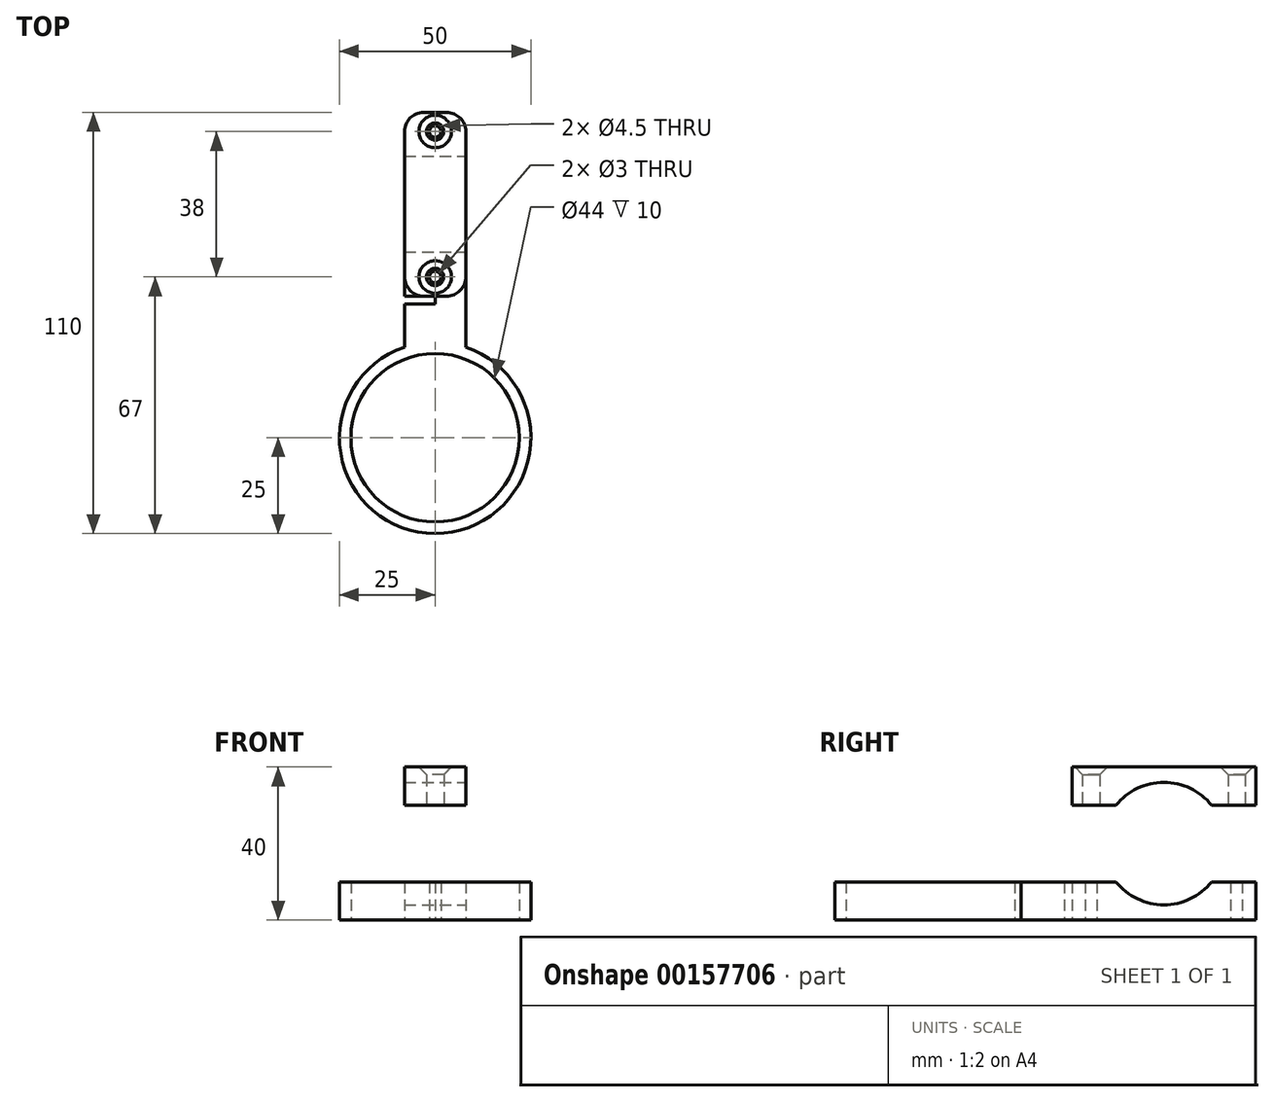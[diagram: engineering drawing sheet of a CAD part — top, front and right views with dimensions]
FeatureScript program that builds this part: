
annotation { "Feature Type Name" : "Feature", "Feature Type Description" : "" }
export const myFeature = defineFeature(function(context is Context, id is Id, definition is map)
    precondition{}
    {
        {
            var Q0;
            Q0=qCreatedBy(makeId("Top.planeOp"),FACE);
            var sketch = newSketch(context, id + "F0", { "sketchPlane" : qUnion([Q0])});
            skCircle(sketch, "E0", {"center": v(0, -25) * mm, "radius": 25 * mm});
            skLineSegment(sketch, "E1", {"start": v(0, 0) * mm, "end": v(0, 10) * mm});
            skLineSegment(sketch, "E2", {"start": v(0, 10) * mm, "end": v(-8, 10) * mm});
            skLineSegment(sketch, "E3", {"start": v(-8, 10) * mm, "end": v(-8, -1.31) * mm});
            skLineSegment(sketch, "E4.MirrorCS", {"start": v(4, 10) * mm, "end": v(8, 10) * mm});
            skLineSegment(sketch, "E5.MirrorCS", {"start": v(8, 10) * mm, "end": v(8, -1.31) * mm});
            skCircle(sketch, "E6", {"center": v(0, -25) * mm, "radius": 22 * mm});
            skLineSegment(sketch, "E7", {"start": v(4, 10) * mm, "end": v(4, -3.37) * mm});
            skLineSegment(sketch, "E8", {"start": v(0, -3) * mm, "end": v(0, 0) * mm});
            skPoint(sketch, "E9", {"position": v(4, 10) * mm});
            skPoint(sketch, "E10.orphan", {"position": v(0, 10) * mm});
            skLineSegment(sketch, "E11.bottom", {"start": v(-8, 10) * mm, "end": v(0, 10) * mm});
            skLineSegment(sketch, "E11.top", {"start": v(-8, 12) * mm, "end": v(0, 12) * mm});
            skLineSegment(sketch, "E11.left", {"start": v(-8, 10) * mm, "end": v(-8, 12) * mm});
            skLineSegment(sketch, "E11.right", {"start": v(0, 10) * mm, "end": v(0, 12) * mm});
            skLineSegment(sketch, "E12.bottom", {"start": v(-8, 12) * mm, "end": v(8, 12) * mm});
            skLineSegment(sketch, "E12.top", {"start": v(-8, 60) * mm, "end": v(8, 60) * mm});
            skLineSegment(sketch, "E12.left", {"start": v(-8, 12) * mm, "end": v(-8, 60) * mm});
            skLineSegment(sketch, "E12.right", {"start": v(8, 12) * mm, "end": v(8, 60) * mm});
            skLineSegment(sketch, "E13", {"start": v(-8, 17) * mm, "end": v(8, 17) * mm});
            skLineSegment(sketch, "E14", {"start": v(-8, 36) * mm, "end": v(8, 36) * mm, "construction": true});
            skLineSegment(sketch, "E15.MirrorCS", {"start": v(-8, 55) * mm, "end": v(8, 55) * mm});
            skCircle(sketch, "E16", {"center": v(0, 55) * mm, "radius": 1.5 * mm});
            skCircle(sketch, "E17.MirrorC", {"center": v(0, 17) * mm, "radius": 1.5 * mm});
            skCircle(sketch, "E18", {"center": v(0, 55) * mm, "radius": 2.25 * mm});
            skCircle(sketch, "E19.MirrorC", {"center": v(0, 17) * mm, "radius": 2.25 * mm});
            skLineSegment(sketch, "E20", {"start": v(8, 10) * mm, "end": v(8, 12) * mm});
            skSolve(sketch);
        }
        {
            var Q0;
            {var subQ0=sQuery(id+"F0.wireOp",EDGE,"E1");Q0=makeQuery(id+"F0.imprint","IMPRINT",FACE,{"disambiguationData":[TD([[makeQuery(id+"F0.imprint","IMPRINT",EDGE,{"derivedFrom":subQ0}),1.0]])]});}
            var Q1;
            {var subQ4=sQuery(id+"F0.wireOp",EDGE,"E4.MirrorCS");Q1=makeQuery(id+"F0.imprint","IMPRINT",FACE,{"disambiguationData":[TD([[makeQuery(id+"F0.imprint","IMPRINT",EDGE,{"derivedFrom":subQ4}),-1.0]])]});}
            var Q2;
            {var subQ3=sQuery(id+"F0.wireOp",EDGE,"E8");Q2=makeQuery(id+"F0.imprint","IMPRINT",FACE,{"disambiguationData":[TD([[makeQuery(id+"F0.imprint","IMPRINT",EDGE,{"derivedFrom":subQ3}),1.0]])]});}
            var Q3;
            {var subQ5=sQuery(id+"F0.wireOp",EDGE,"E1");Q3=makeQuery(id+"F0.imprint","IMPRINT",FACE,{"disambiguationData":[TD([[makeQuery(id+"F0.imprint","IMPRINT",EDGE,{"derivedFrom":subQ5}),-1.0]])]});}
            var Q4;
            {var subQ0=sQuery(id+"F0.wireOp",EDGE,"E8");Q4=makeQuery(id+"F0.imprint","IMPRINT",FACE,{"disambiguationData":[TD([[makeQuery(id+"F0.imprint","IMPRINT",EDGE,{"derivedFrom":subQ0}),-1.0]])]});}
            extrude(context, id + "F1", {"entities" : qUnion([Q0, Q1, Q2, Q3, Q4]), "depth" : 10 * mm, "offsetDistance" : 25 * mm});
        }
        {
            var Q0;
            {var subQ0=sQuery(id+"F0.wireOp",EDGE,"E12.top");Q0=makeQuery(id+"F0.imprint","IMPRINT",FACE,{"disambiguationData":[TD([[makeQuery(id+"F0.imprint","IMPRINT",EDGE,{"derivedFrom":subQ0}),-1.0]])]});}
            var Q1;
            {var subQ0=sQuery(id+"F0.wireOp",EDGE,"E13");Q1=makeQuery(id+"F0.imprint","IMPRINT",FACE,{"disambiguationData":[TD([[makeQuery(id+"F0.imprint","IMPRINT",EDGE,{"derivedFrom":subQ0}),1.0]])]});}
            var Q2;
            {var subQ3=sQuery(id+"F0.wireOp",EDGE,"E13");Q2=makeQuery(id+"F0.imprint","IMPRINT",FACE,{"disambiguationData":[TD([[makeQuery(id+"F0.imprint","IMPRINT",EDGE,{"derivedFrom":subQ3}),-1.0]])]});}
            var Q3;
            Q3=makeQuery(id+"F0.imprint","IMPRINT",FACE,{"disambiguationData":[TD([[makeQuery(id+"F0.imprint","IMPRINT",EDGE,{"derivedFrom":sQuery(id+"F0.wireOp",EDGE,"E11.bottom")}),1.0]])]});
            var Q4;
            {var subQ0=sQuery(id+"F0.wireOp",EDGE,"E18");var subQ1=sQuery(id+"F0.wireOp",EDGE,"E15.MirrorCS");var subQ2=makeQuery(id+"F0.imprint","INTERSECT",VERTEX,{"disambiguationData":[OD(0.0)],"derivedFrom":[subQ1,subQ0]});Q4=makeQuery(id+"F0.imprint","IMPRINT",FACE,{"disambiguationData":[TD([[makeQuery(id+"F0.imprint","IMPRINT",EDGE,{"disambiguationData":[TD([[subQ2,-1.0]])],"derivedFrom":subQ1}),-1.0]])]});}
            var Q5;
            {var subQ0=sQuery(id+"F0.wireOp",EDGE,"E18");var subQ1=sQuery(id+"F0.wireOp",EDGE,"E15.MirrorCS");var subQ2=makeQuery(id+"F0.imprint","INTERSECT",VERTEX,{"disambiguationData":[OD(0.0)],"derivedFrom":[subQ1,subQ0]});Q5=makeQuery(id+"F0.imprint","IMPRINT",FACE,{"disambiguationData":[TD([[makeQuery(id+"F0.imprint","IMPRINT",EDGE,{"disambiguationData":[TD([[subQ2,-1.0]])],"derivedFrom":subQ1}),1.0]])]});}
            var Q6;
            {var subQ0=sQuery(id+"F0.wireOp",EDGE,"E13");var subQ10=sQuery(id+"F0.wireOp",EDGE,"E12.left");var subQ11=makeQuery(id+"F0.imprint","INTERSECT",VERTEX,{"derivedFrom":[subQ10,subQ0]});Q6=makeQuery(id+"F0.imprint","IMPRINT",FACE,{"disambiguationData":[TD([[makeQuery(id+"F0.imprint","IMPRINT",EDGE,{"disambiguationData":[TD([[subQ11,-1.0]])],"derivedFrom":subQ10}),-1.0]])]});}
            var Q7;
            {var subQ1=sQuery(id+"F0.wireOp",EDGE,"E12.bottom");var subQ11=makeQuery(id+"F0.imprint","INTERSECT",VERTEX,{"derivedFrom":[sQuery(id+"F0.wireOp",EDGE,"E11.right"),subQ1]});Q7=makeQuery(id+"F0.imprint","IMPRINT",FACE,{"disambiguationData":[TD([[makeQuery(id+"F0.imprint","IMPRINT",EDGE,{"disambiguationData":[TD([[subQ11,-1.0]])],"derivedFrom":subQ1}),1.0]])]});}
            extrude(context, id + "F2", {"entities" : qUnion([Q0, Q1, Q2, Q3, Q4, Q5, Q6, Q7]), "operationType" : NewBodyOperationType.ADD, "depth" : 10 * mm});
        }
        {
            var Q0;
            {var subQ1=sQuery(id+"F0.wireOp",EDGE,"E12.bottom");var subQ11=makeQuery(id+"F0.imprint","INTERSECT",VERTEX,{"derivedFrom":[sQuery(id+"F0.wireOp",EDGE,"E11.right"),subQ1]});Q0=makeQuery(id+"F0.imprint","IMPRINT",FACE,{"disambiguationData":[TD([[makeQuery(id+"F0.imprint","IMPRINT",EDGE,{"disambiguationData":[TD([[subQ11,-1.0]])],"derivedFrom":subQ1}),1.0]])]});}
            var Q1;
            {var subQ0=sQuery(id+"F0.wireOp",EDGE,"E13");var subQ8=sQuery(id+"F0.wireOp",EDGE,"E12.left");var subQ9=makeQuery(id+"F0.imprint","INTERSECT",VERTEX,{"derivedFrom":[subQ8,subQ0]});Q1=makeQuery(id+"F0.imprint","IMPRINT",FACE,{"disambiguationData":[TD([[makeQuery(id+"F0.imprint","IMPRINT",EDGE,{"disambiguationData":[TD([[subQ9,-1.0]])],"derivedFrom":subQ8}),-1.0]])]});}
            var Q2;
            {var subQ1=sQuery(id+"F0.wireOp",EDGE,"E12.top");Q2=makeQuery(id+"F0.imprint","IMPRINT",FACE,{"disambiguationData":[TD([[makeQuery(id+"F0.imprint","IMPRINT",EDGE,{"derivedFrom":subQ1}),-1.0]])]});}
            extrude(context, id + "F3", {"entities" : qUnion([Q0, Q1, Q2]), "depth" : 40 * mm, "hasSecondDirection" : true, "secondDirectionOppositeDirection" : false, "secondDirectionDepth" : 30 * mm});
        }
        {
            var Q0;
            Q0=qCreatedBy(makeId("Right.planeOp"),FACE);
            var sketch = newSketch(context, id + "F4", { "sketchPlane" : qUnion([Q0])});
            skCircle(sketch, "E21", {"center": v(36, 20) * mm, "radius": 16 * mm});
            skSolve(sketch);
        }
        {
            var Q0;
            Q0=makeQuery(id+"F4.imprint","IMPRINT",FACE,{"disambiguationData":[TD([[makeQuery(id+"F4.imprint","IMPRINT",EDGE,{"derivedFrom":sQuery(id+"F4.wireOp",EDGE,"E21")}),1.0]])]});
            extrude(context, id + "F5", {"entities" : qUnion([Q0]), "operationType" : NewBodyOperationType.REMOVE, "oppositeDirection" : true, "depth" : 25 * mm, "hasSecondDirection" : true, "secondDirectionOppositeDirection" : false, "secondDirectionDepth" : 25 * mm});
        }
        {
            var Q0;
            Q0=makeQuery(id+"F4.imprint","IMPRINT",FACE,{"disambiguationData":[TD([[makeQuery(id+"F4.imprint","IMPRINT",EDGE,{"derivedFrom":sQuery(id+"F4.wireOp",EDGE,"E21")}),1.0]])]});
            extrude(context, id + "F6", {"entities" : qUnion([Q0]), "operationType" : NewBodyOperationType.REMOVE, "depth" : 25 * mm, "hasSecondDirection" : true, "secondDirectionOppositeDirection" : true, "secondDirectionDepth" : 25 * mm});
        }
        {
            var Q0;
            Q0=makeQuery(id+"F3.opExtrude","CAP_EDGE",EDGE,{"disambiguationData":[OSD([sQuery(id+"F0.wireOp",EDGE,"E19.MirrorC")])],"isStart":false});
            var Q1;
            Q1=makeQuery(id+"F3.opExtrude","CAP_EDGE",EDGE,{"disambiguationData":[OSD([sQuery(id+"F0.wireOp",EDGE,"E18")])],"isStart":false});
            chamfer(context, id + "F7", {"entities" : qUnion([Q0, Q1]), "width" : 2 * mm, "tangentPropagation" : true});
        }
        {
            var Q0;
            Q0=makeQuery(id+"F3.opExtrude","SWEPT_EDGE",EDGE,{"disambiguationData":[OSD([sQuery(id+"F0.wireOp",EDGE,"E12.bottom"),sQuery(id+"F0.wireOp",EDGE,"E12.right"),sQuery(id+"F0.wireOp",EDGE,"E20")])]});
            var Q1;
            Q1=makeQuery(id+"F3.opExtrude","SWEPT_EDGE",EDGE,{"disambiguationData":[OSD([sQuery(id+"F0.wireOp",EDGE,"E11.left"),sQuery(id+"F0.wireOp",EDGE,"E12.bottom"),sQuery(id+"F0.wireOp",EDGE,"E12.left")])]});
            var Q2;
            Q2=makeQuery(id+"F3.opExtrude","SWEPT_EDGE",EDGE,{"disambiguationData":[OSD([sQuery(id+"F0.wireOp",EDGE,"E12.top"),sQuery(id+"F0.wireOp",EDGE,"E12.left")])]});
            var Q3;
            Q3=makeQuery(id+"F3.opExtrude","SWEPT_EDGE",EDGE,{"disambiguationData":[OSD([sQuery(id+"F0.wireOp",EDGE,"E12.top"),sQuery(id+"F0.wireOp",EDGE,"E12.right")])]});
            var Q4;
            Q4=makeQuery(id+"F2.opExtrude","SWEPT_EDGE",EDGE,{"disambiguationData":[OSD([sQuery(id+"F0.wireOp",EDGE,"E12.top"),sQuery(id+"F0.wireOp",EDGE,"E12.left")])]});
            var Q5;
            Q5=makeQuery(id+"F2.opExtrude","SWEPT_EDGE",EDGE,{"disambiguationData":[OSD([sQuery(id+"F0.wireOp",EDGE,"E12.top"),sQuery(id+"F0.wireOp",EDGE,"E12.right")])]});
            fillet(context, id + "F8", {"entities" : qUnion([Q0, Q1, Q2, Q3, Q4, Q5]), "radius" : 5 * mm, "tangentPropagation" : true, "allowEdgeOverflow" : false});
        }
    });
